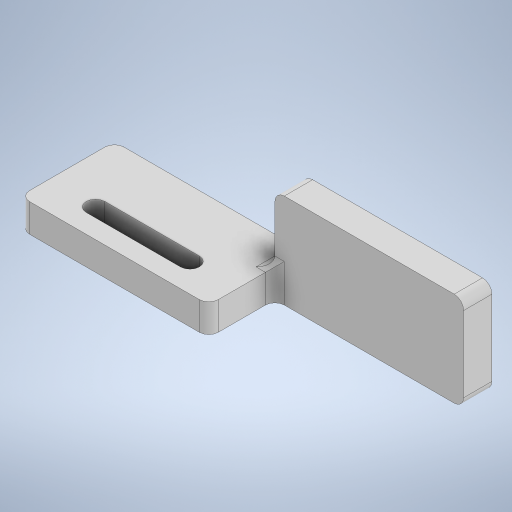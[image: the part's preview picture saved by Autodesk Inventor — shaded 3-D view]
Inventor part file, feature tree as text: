
AUTODESK INVENTOR PART (.ipt)
format: ipt  version: 2023 (Build 270158000, 158)  size: 258,560 bytes
history: native  units: mm
features: fillet x3, extrude x2, sketch x2
ambient origin geometry x8: Origin, YZ Plane, XZ Plane, XY Plane, X Axis, Y Axis, Z Axis, Center Point
bodies: Solid1 (feature_tree)
feature tree (7):
  extrude  "Extrusion1"  Depth=10.0mm
  extrude  "Extrusion2"  Depth=10.0mm
  fillet  "Fillet1"  Radius=3.0mm
  fillet  "Fillet2"  Radius=10.0mm
  fillet  "Fillet3"  Radius=20.0mm
  sketch  "Sketch1"  dims[d0=20.0mm d1=10.0mm]
  sketch  "Sketch2"  dims[d2=2.0mm d3=10.0mm d4=3.0mm d5=0.0mm d6=10.0mm d7=20.0mm d8=3.0mm d9=0.0mm d10=2.0mm d11=1.0mm d12=1.0mm d13=1.0mm d14=0.0mm]
